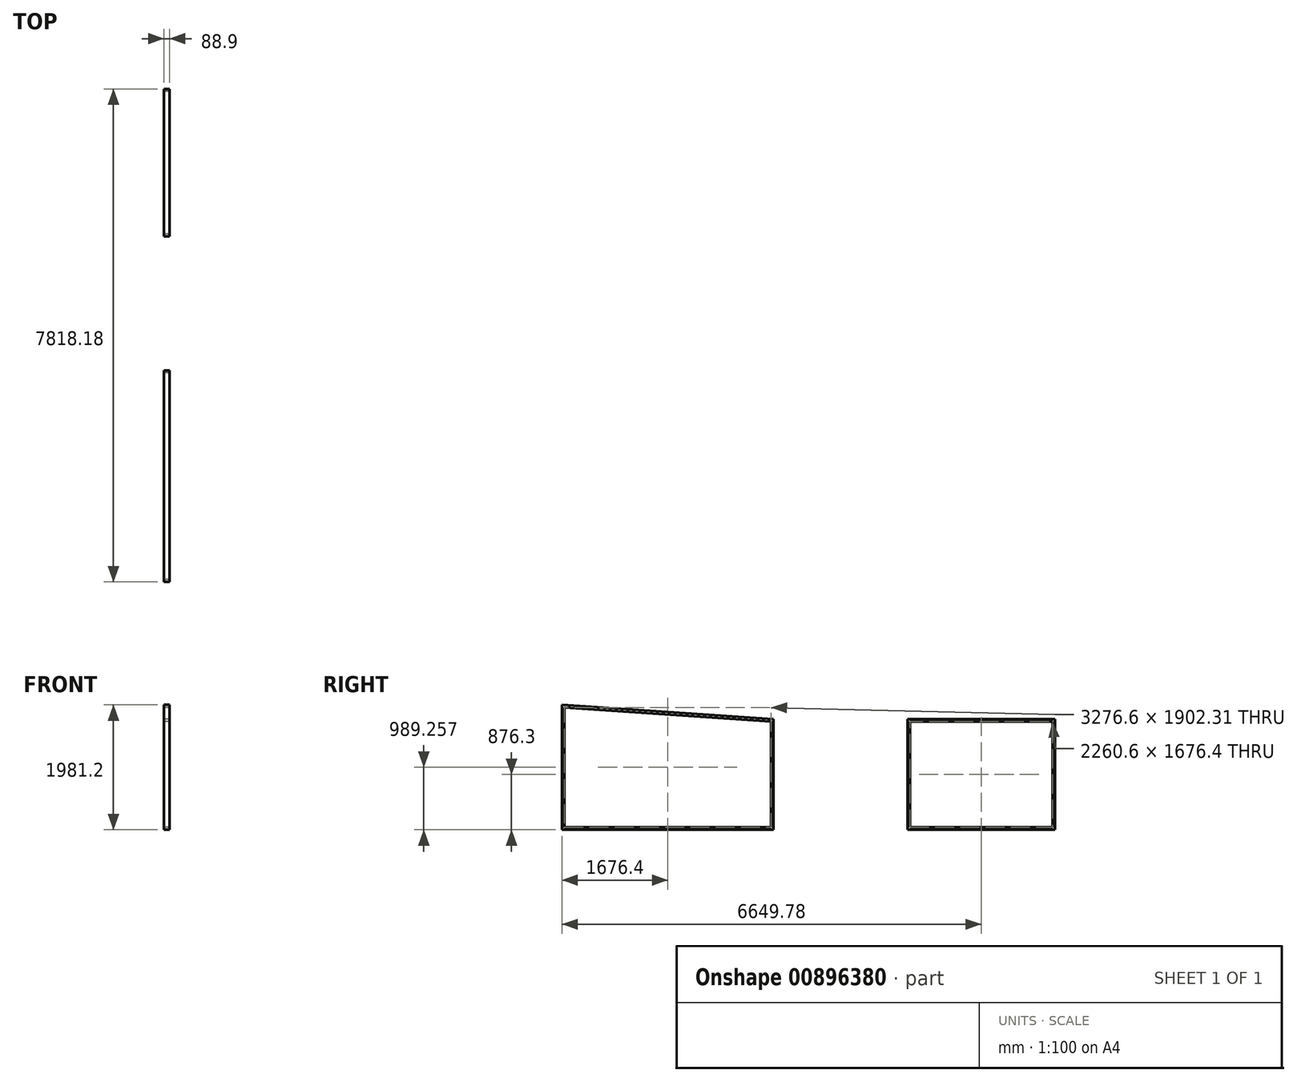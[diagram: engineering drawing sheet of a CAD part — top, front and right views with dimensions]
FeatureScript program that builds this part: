
annotation { "Feature Type Name" : "Feature", "Feature Type Description" : "" }
export const myFeature = defineFeature(function(context is Context, id is Id, definition is map)
    precondition{}
    {
        {
            var Q0;
            Q0=qCreatedBy(makeId("Right.planeOp"),FACE);
            var sketch = newSketch(context, id + "F0", { "sketchPlane" : qUnion([Q0])});
            skLineSegment(sketch, "E0.top", {"start": v(-3352.8, 0) * mm, "end": v(0, 0) * mm});
            skLineSegment(sketch, "E0.left", {"start": v(-3352.8, 1981.2) * mm, "end": v(-3352.8, 0) * mm});
            skLineSegment(sketch, "E0.right", {"start": v(0, 1752.6) * mm, "end": v(0, 0) * mm});
            skLineSegment(sketch, "E1", {"start": v(-3352.8, 1981.2) * mm, "end": v(0, 1752.6) * mm});
            skLineSegment(sketch, "E2.0", {"start": v(-3314.7, 1940.41) * mm, "end": v(-38.1, 1717) * mm});
            skLineSegment(sketch, "E2.1", {"start": v(-3314.7, 1940.41) * mm, "end": v(-3314.7, 38.1) * mm});
            skLineSegment(sketch, "E2.2", {"start": v(-3314.7, 38.1) * mm, "end": v(-38.1, 38.1) * mm});
            skLineSegment(sketch, "E2.3", {"start": v(-38.1, 1717) * mm, "end": v(-38.1, 38.1) * mm});
            skLineSegment(sketch, "E3.bottom", {"start": v(4465.38, 0) * mm, "end": v(2128.58, 0) * mm});
            skLineSegment(sketch, "E3.top", {"start": v(4465.38, 1752.6) * mm, "end": v(2128.58, 1752.6) * mm});
            skLineSegment(sketch, "E3.left", {"start": v(4465.38, 0) * mm, "end": v(4465.38, 1752.6) * mm});
            skLineSegment(sketch, "E3.right", {"start": v(2128.58, 0) * mm, "end": v(2128.58, 1752.6) * mm});
            skLineSegment(sketch, "E4.0", {"start": v(4427.28, 38.1) * mm, "end": v(2166.68, 38.1) * mm});
            skLineSegment(sketch, "E4.1", {"start": v(4427.28, 38.1) * mm, "end": v(4427.28, 1714.5) * mm});
            skLineSegment(sketch, "E4.2", {"start": v(4427.28, 1714.5) * mm, "end": v(2166.68, 1714.5) * mm});
            skLineSegment(sketch, "E4.3", {"start": v(2166.68, 38.1) * mm, "end": v(2166.68, 1714.5) * mm});
            skSolve(sketch);
        }
        {
            var Q0;
            Q0 = qSketchRegion(id + "F0", true);
            extrude(context, id + "F1", {"entities" : qUnion([Q0]), "depth" : 88.9 * mm, "offsetDistance" : 25.4 * mm});
        }
    });
